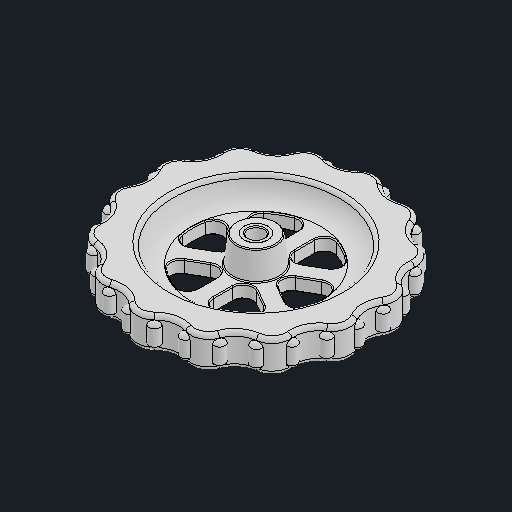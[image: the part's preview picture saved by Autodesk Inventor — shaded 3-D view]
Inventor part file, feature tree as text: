
AUTODESK INVENTOR PART (.ipt)
format: ipt  version: 2024.2 (Build 282272000, 272)  size: 907,776 bytes
history: native  units: mm
features: other x2, chamfer x1, pattern_circular x1
ambient origin geometry x8: Origin, YZ Plane, XZ Plane, XY Plane, X Axis, Y Axis, Z Axis, Center Point
bodies: Body1 (feature_tree), Body2 (feature_tree)
feature tree (4):
  other  "솔리드1"
  other  "솔리드2"
  chamfer  "Chamfer1"  [1 undecoded]
  pattern_circular  "CirPattern5"
note: 1 required parameter value undecoded (feature->parameter linkage not recoverable at this tier; creation-order binding heuristic only, values carry confidence <= 0.55)
